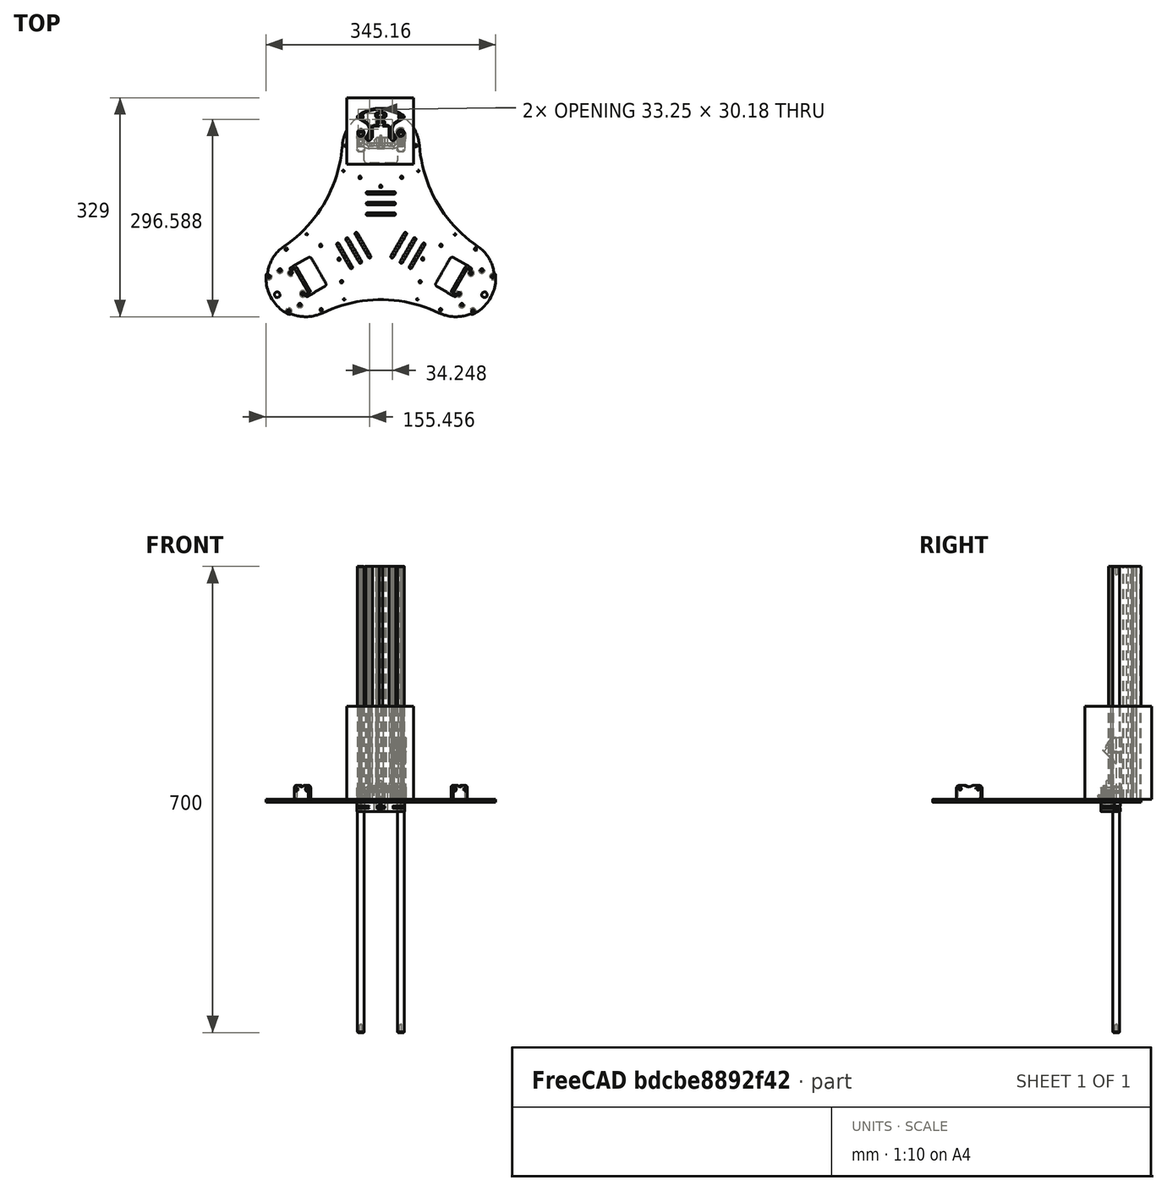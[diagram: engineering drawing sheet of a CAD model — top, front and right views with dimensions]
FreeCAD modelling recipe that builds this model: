
FCSTD DOCUMENT  (FreeCAD 0.18R16146 (Git))
Label: Vertical-Slider_w_FlyingExtruder
License: All rights reserved
LicenseURL: http://en.wikipedia.org/wiki/All_rights_reserved
objects: Part::FeaturePython×10, Part::Feature×9, App::Part×5, Sketcher::SketchObject×4, PartDesign::Plane×3, PartDesign::Body×3, Spreadsheet::Sheet×2, PartDesign::Revolution×1, Part::Box×1, Part::Compound×1, App::DocumentObjectGroup×1, PartDesign::Point×1, PartDesign::AdditiveLoft×1, Part::Mirroring×1, PartDesign::Hole×1, PartDesign::FeatureBase×1
note: 40 computed .brp shape members not serialized (recipe doc carries the construction recipe); baked Part::Feature solids carry a one-line shape summary decoded from their .brp

FEATURE [Part::Feature] K8800_BAP
  Placement = pos=(0,-153,-2) rot=(0,0,1;0rad)
  shape: bbox 351.2 x 331.3 x 25.02 mm, 225 faces (baked)
FEATURE [Part::Feature] K8800_RD10  label="K8800_RodLeft"
  Placement = pos=(-30,0,0) rot=(0,0,1;0rad)
  shape: bbox 10 x 10 x 700 mm, 9 faces (baked)
FEATURE [Part::Feature] K8800_RD011  label="K8800_RodRight"
  Placement = pos=(30,0,0) rot=(0,0,1;0rad)
  shape: bbox 10 x 10 x 700 mm, 9 faces (baked)
FEATURE [Part::Feature] K8800_RI
  shape: bbox 70.64 x 62.27 x 700 mm, 164 faces (baked)
FEATURE [Part::Feature] K8800_VS
  Placement = pos=(0,0,0) rot=(0,0,1;1.5708rad)
  shape: bbox 72.01 x 24.93 x 46.6 mm, 535 faces (baked)
FEATURE [Part::Feature] K8800_LB10  label="K8800_LB10-L"
  Placement = pos=(-30,0,0) rot=(0,0,1;0rad)
  shape: bbox 12 x 12 x 36 mm, 16 faces (baked)
FEATURE [Part::Feature] K8800_LB10001  label="K8800_LB10-R"
  Placement = pos=(30,0,0) rot=(0,0,1;0rad)
  shape: bbox 12 x 12 x 36 mm, 16 faces (baked)
FEATURE [Spreadsheet::Sheet] Spreadsheet  label="Schrauben"
  cells = A1(M5RadiusBore)==2.5mm; B1=M5RadiusBore; C1=Radius der Bohrungen für M5-Schrauben; A2(M5HexNutWidth)==8mm; B2=M5HexNutWidth; C2=Schlüsselweite der M5-Muttern; A3(M5HexNutHeight)==4mm; B3=M5HexNutHeight; C3=Höhe der M5-Muttern; A4(M5HexHeadRadius)==4.7mm; B4=M5HexHeadRadius; C4=Radius des Schraubenkopfes; A5(M5HexHeadHeight)==5.1mm; B5=M5HexHeadHeight; C5=Höhe des Schraubenkopfes; A6(M5InsertHeight)==6mm; B6=M5InsertHeight; C6=Höhe des Insert; A7(M5InserWidth)==6.3mm; B7=M5InserWidth; C7=Durchmesser (Taille) des Insert; A8(MCThreadLength)==8.25mm; B8=MCThreadLength; C8=Gewindelänge der Magnetic Cups; A9(MCHeadHeight)==4.8mm; B9=MCHeadHeight; C9=Kopfhöhe der Magentic Cups; A10(MCHeadRadius)==8.5mm / 2; B10=MCHeadRadius; C10=Radius des Magnetic Cups
FEATURE [Spreadsheet::Sheet] Spreadsheet001  label="Global"
  cells = A1===========; B1=3D Druckparameter; C1===================================; A2(NozzleSize)==0.6mm; B2=NozzleSize; C2=Düsendurchmesser; A3(ExtMult)=0.9; B3=ExtMult; C3=Extrusion Multiplier; A4(NozzleWidth)==NozzleSize * ExtMult; B4=NozzeWidth; C4=Extrusion width; A5(numPerimeter)=3; B5=numPerimeter; C5=Anzahl der Perimeter; A6(Flesh)==2 * NozzleWidth; B6=Flesh; C6=Zusätzlicher Material; A7===========; B7=Bronzelager; C7===================================; A8(bearingID)==10mm; B8=bearingID; C8=Innendurchmesser Lager; A9(bearingOD)==13mm; B9=bearingOD; C9=Außendurchmesser Lager; A10(bearingLen)==20mm; B10=bearingLen; C10=Länge des Lagers; A11===========; B11=Mechanik Lager; C11===================================; A12(distRods)==60mm; B12=distRods; C12=Abstand der Wellen; A13(diaRods)==10mm; B13=diaRods; C13=Durchmesser der Wellen; A14(clearanceRods)==NozzleWidth / 2; B14=clearanceRods; C14=Sicherheitsabstand für diaRods; A15===========; B15=Laufbuchse; C15===================================; A16(bushingShrink)==NozzleWidth / 2; B16=bushingShrink; C16=radiale Schrumpfung für Laufbuchsen-Pressung; A17(bushingID)==bearingOD; B17=bushingID; C17=Innendurchmesser Laufbuchse; A18(bushingID3D)==bushingID - 2 * bushingShrink; B18=bushingID3D; C18=zu druckender Innendurchmesser Laufbuchse; A19(bushingOD3D)==bushingID3D + numPerimeter * NozzleWidth * 2; B19=bushingOD3D; C19=zu druckender Außendurchmesser Laufbuchse; A20(bushingIR3D)==bushingID3D / 2; B20=bushingIR3D; C20=effektiver innerer Radius der Laufbuchse; A21(bushingOR3D)==bushingOD3D / 2; B21=bushingOR3D; C21=effektiver äußerer Radius der Laufbuchse; A22(bushingWallTickness)==numPerimeter * NozzleWidth; B22=bushingWallTickness; C22=Wanddicke Laufbuchse; A23(bushingLength)==90mm; B23=bushingLength; C23=Gesamtlänge der Linearführung; A24(bushingRotArc)==300°; B24=bushingRotArc; C24=Rotationswinkel für Extrusion; A25===========; B25=Vertical Slider; C25===================================; A32===========; C32===================================; A33===========; C33===================================; A34===========; C34===================================; A35===========; C35===================================; A36===========; C36===================================; A37===========; C37===================================
FEATURE [Part::Feature] K8800_MC  label="K8800_MC-L"
  Placement = pos=(-30,-18,-3.1e-15) rot=(1,0,0;1.5708rad)
  shape: bbox 8.5 x 12.91 x 8.5 mm, 20 faces (baked)
FEATURE [Part::Feature] K8800_MC001  label="K8800_MC-R"
  Placement = pos=(30,-18,-3.1e-15) rot=(1,0,0;1.5708rad)
  shape: bbox 8.5 x 12.91 x 8.5 mm, 20 faces (baked)
FEATURE [Sketcher::SketchObject] Sketch
  MapMode = 5
  Placement = pos=(0,0,0) rot=(1,0,0;1.5708rad)
  Support = -> [XZ_Plane003]
  expr: Constraints[12] = <<Global>>.bushingWallTickness
  expr: Constraints[11] = <<Global>>.bushingWallTickness
  sketch-geometry (13):
    g0: LineSegment [constr] StartX=0 StartY=50 StartZ=0 EndX=0 EndY=-50 EndZ=0
    g1: LineSegment StartX=-6.23 StartY=48.24 StartZ=0 EndX=-6.23 EndY=27.16 EndZ=0
    g2: LineSegment StartX=-7.85 StartY=48.24 StartZ=0 EndX=-7.85 EndY=27.16 EndZ=0
    g3: LineSegment StartX=-5.54 StartY=25 StartZ=0 EndX=-5.54 EndY=-25 EndZ=0
    g4: LineSegment StartX=-7.16 StartY=25 StartZ=0 EndX=-7.16 EndY=-25 EndZ=0
    g5: LineSegment StartX=-7.85 StartY=-27.16 StartZ=0 EndX=-7.85 EndY=-48.24 EndZ=0
    g6: LineSegment StartX=-6.23 StartY=-27.16 StartZ=0 EndX=-6.23 EndY=-48.24 EndZ=0
    g7: LineSegment StartX=-7.85 StartY=-48.24 StartZ=0 EndX=-6.23 EndY=-48.24 EndZ=0
    g8: LineSegment StartX=-7.85 StartY=48.24 StartZ=0 EndX=-6.23 EndY=48.24 EndZ=0
    g9: LineSegment StartX=-7.85 StartY=27.16 StartZ=0 EndX=-7.16 EndY=25 EndZ=0
    g10: LineSegment StartX=-6.23 StartY=27.16 StartZ=0 EndX=-5.54 EndY=25 EndZ=0
    g11: LineSegment StartX=-7.16 StartY=-25 StartZ=0 EndX=-7.85 EndY=-27.16 EndZ=0
    g12: LineSegment StartX=-5.54 StartY=-25 StartZ=0 EndX=-6.23 EndY=-27.16 EndZ=0
  constraints (39):
    c: Vertical(g0)
    c: DistanceY(g0,g0) = 100
    c: Symmetric(g0,g0,g-1)
    c: Vertical(g1)
    c: Vertical(g2)
    c: Vertical(g3)
    c: Vertical(g4)
    c: Vertical(g5)
    c: Vertical(g6)
    c: Horizontal(g7)
    c: Perpendicular(g8,g0)
    c: DistanceX(g8,g8) = 1.62
    c: DistanceX(g7,g7) = 1.62
    c: Coincident(g7,g6)
    c: Coincident(g7,g5)
    c: Coincident(g2,g8)
    c: Coincident(g1,g8)
    c: DistanceX(g4,g3) = 1.62
    c: DistanceY(g2,g2) = 21.08  'upperBushingLeft'
    c: DistanceY(g1,g1) = 21.08  'upperBushingRight'
    c: DistanceY(g5,g5) = 21.08  'lowerBushingLeft'
    c: DistanceY(g6,g6) = 21.08  'lowerBushingRight'
    c: DistanceY(g4,g4) = 50
    c: Equal(g4,g3)
    c: DistanceY(g3,g-1) = 25
    c: DistanceY(g4,g-1) = 25
    c: DistanceX(g1,g0) = 6.23
    c: DistanceX(g6,g-1) = 6.23
    c: DistanceY(g3,g1) = 2.16
    c: Coincident(g1,g10)
    c: Coincident(g10,g3)
    c: Coincident(g9,g2)
    c: Coincident(g9,g4)
    c: DistanceY(g12,g12) = 2.16
    c: Coincident(g12,g3)
    c: Coincident(g11,g4)
    c: DistanceX(g3,g-1) = 5.54
    c: Coincident(g12,g6)
    c: Coincident(g11,g5)
FEATURE [PartDesign::Revolution] Revolution
  Angle = 300
  Axis = (0,-2e-16,1)
  Base = (0,0,0)
  Placement = pos=(0,0,0) rot=(1,0,0;1.5708rad)
  Profile = -> Sketch
  ReferenceAxis = -> Sketch [V_Axis]
  expr: Angle = <<Global>>.bushingRotArc
FEATURE [App::Part] Part003  label="Velleman CAD"
  Group = -> [K8800_VS,K8800_LB10,K8800_LB10001,K8800_MC,K8800_MC001]
  Origin = -> Origin005
FEATURE [App::Part] Part  label="K8800-VerticalSlider"
  Group = -> [Part003]
  Origin = -> Origin
FEATURE [Part::Box] Box  label="Cube"
  AttacherType = Attacher::AttachEngine3D
  Height = 140
  Length = 100
  Placement = pos=(-51,-47,0) rot=(0,0,1;0rad)
  Width = 100
FEATURE [App::Part] Part004  label="Velleman CAD001"
  Origin = -> Origin006
FEATURE [Part::Compound] Compound
  Links = -> [K8800_RI,K8800_RD011,K8800_RD10]
FEATURE [Part::FeaturePython] Slice  # WARN: FeaturePython — macro-defined, semantics opaque (R4)
  Base = -> Compound
  Mode = 1
  Tolerance = 0
  Tools = -> [Box]
  Visibility1 = false
FEATURE [Part::FeaturePython] Slice_child0  label="Slice.0"  # WARN: FeaturePython — macro-defined, semantics opaque (R4)
  Base = -> Slice
  FilterType = 1
  Invert = false
  OverrideMaxVal = 0
  Visibility1 = false
  WindowFrom = 80
  WindowTo = 100
  items = 0
FEATURE [Part::FeaturePython] Slice_child1  label="Slice.1"  # WARN: FeaturePython — macro-defined, semantics opaque (R4)
  Base = -> Slice
  FilterType = 1
  Invert = false
  OverrideMaxVal = 0
  Visibility1 = true
  WindowFrom = 80
  WindowTo = 100
  items = 1
FEATURE [Part::FeaturePython] Slice_child2  label="Slice.2"  # WARN: FeaturePython — macro-defined, semantics opaque (R4)
  Base = -> Slice
  FilterType = 1
  Invert = false
  OverrideMaxVal = 0
  Visibility1 = false
  WindowFrom = 80
  WindowTo = 100
  items = 2
FEATURE [Part::FeaturePython] Slice_child3  label="Slice.3"  # WARN: FeaturePython — macro-defined, semantics opaque (R4)
  Base = -> Slice
  FilterType = 1
  Invert = false
  OverrideMaxVal = 0
  Visibility1 = false
  WindowFrom = 80
  WindowTo = 100
  items = 3
FEATURE [Part::FeaturePython] Slice_child4  label="Slice.4"  # WARN: FeaturePython — macro-defined, semantics opaque (R4)
  Base = -> Slice
  FilterType = 1
  Invert = false
  OverrideMaxVal = 0
  Visibility1 = true
  WindowFrom = 80
  WindowTo = 100
  items = 4
FEATURE [Part::FeaturePython] Slice_child5  label="Slice.5"  # WARN: FeaturePython — macro-defined, semantics opaque (R4)
  Base = -> Slice
  FilterType = 1
  Invert = false
  OverrideMaxVal = 0
  Visibility1 = false
  WindowFrom = 80
  WindowTo = 100
  items = 5
FEATURE [Part::FeaturePython] Slice_child6  label="Slice.6"  # WARN: FeaturePython — macro-defined, semantics opaque (R4)
  Base = -> Slice
  FilterType = 1
  Invert = false
  OverrideMaxVal = 0
  Visibility1 = false
  WindowFrom = 80
  WindowTo = 100
  items = 6
FEATURE [Part::FeaturePython] Slice_child7  label="Slice.7"  # WARN: FeaturePython — macro-defined, semantics opaque (R4)
  Base = -> Slice
  FilterType = 1
  Invert = false
  OverrideMaxVal = 0
  Visibility1 = true
  WindowFrom = 80
  WindowTo = 100
  items = 7
FEATURE [Part::FeaturePython] Slice_child8  label="Slice.8"  # WARN: FeaturePython — macro-defined, semantics opaque (R4)
  Base = -> Slice
  FilterType = 1
  Invert = false
  OverrideMaxVal = 0
  Visibility1 = false
  WindowFrom = 80
  WindowTo = 100
  items = 8
FEATURE [App::DocumentObjectGroup] GrExplode_Slice  label="Exploded Slice"
  Group = -> [Slice_child0,Slice_child1,Slice_child2,Slice_child3,Slice_child4,Slice_child5,Slice_child6,Slice_child7,Slice_child8]
FEATURE [App::Part] Part001  label="VerticalRods"
  Group = -> [Part004,Box,K8800_RI,K8800_RD011,K8800_RD10,Compound,Slice,Slice_child1,Slice_child7,Slice_child6,Slice_child0,Slice_child2,Slice_child3,Slice_child5,Slice_child4,Slice_child8,GrExplode_Slice]
  Origin = -> Origin001
  Placement = pos=(0,0,-20) rot=(0,0,1;0rad)
FEATURE [Sketcher::SketchObject] Sketch004
  AttachmentOffset = pos=(0,1,7.85) rot=(0,0,1;0rad)
  MapMode = 5
  Placement = pos=(0,-7.85,1) rot=(1,0,0;1.5708rad)
  Support = -> [XZ_Plane022]
  sketch-geometry (5):
    g0: Ellipse CenterX=-30 CenterY=66 CenterZ=0 NormalX=0 NormalY=0 NormalZ=1 MajorRadius=16 MinorRadius=7 AngleXU=-1.5708
    g1: LineSegment [constr] StartX=-30 StartY=50 StartZ=0 EndX=-30 EndY=82 EndZ=0
    g2: LineSegment [constr] StartX=-23 StartY=66 StartZ=0 EndX=-37 EndY=66 EndZ=0
    g3: GeomPoint X=-30 Y=51.6125 Z=0
    g4: GeomPoint X=-30 Y=80.3875 Z=0
  constraints (6):
    c: InternalAlignment(g1-g4 -> g0) x4
    c: DistanceX(g0,g-1) = 30
    c: DistanceX(g2,g2) = 14
    c: DistanceY(g1,g1) = 32
    c: DistanceY(g-1,g2) = 66
    c: Parallel(g1,g-2)
FEATURE [PartDesign::Point] DatumPoint
  AttacherType = Attacher::AttachEnginePoint
  MapMode = 37
  Placement = pos=(-30,-7.85,67.045) rot=(0,0,1;0rad)
  Support = -> [Sketch004]
FEATURE [Sketcher::SketchObject] Sketch005
  ExternalGeometry = -> [DatumPoint]
  MapMode = 5
  Placement = pos=(0,0,0) rot=(1,0,0;1.5708rad)
  Support = -> [XZ_Plane022]
  expr: Constraints[7] = Global.distRods / 2
  expr: Constraints[6] = <<Global>>.bushingOD3D - 1.5mm
  sketch-geometry (5):
    g0: LineSegment StartX=-37.1 StartY=83.045 StartZ=0 EndX=-22.9 EndY=83.045 EndZ=0
    g1: LineSegment StartX=-22.9 StartY=83.045 StartZ=0 EndX=-22.9 EndY=43.045 EndZ=0
    g2: LineSegment StartX=-22.9 StartY=43.045 StartZ=0 EndX=-37.1 EndY=43.045 EndZ=0
    g3: LineSegment StartX=-37.1 StartY=43.045 StartZ=0 EndX=-37.1 EndY=83.045 EndZ=0
    g4: LineSegment [constr] StartX=-30 StartY=83.045 StartZ=0 EndX=-30 EndY=32.845 EndZ=0
  constraints (14):
    c: Coincident(g0,g1)
    c: Coincident(g1,g2)
    c: Coincident(g2,g3)
    c: Coincident(g3,g0)
    c: Horizontal(g2)
    c: Vertical(g1)
    c: DistanceX(g0,g0) = 14.2
    c: DistanceX(g4,g-1) = 30
    c: Symmetric(g1,g2,g4)
    c: Symmetric(g0,g0,g4)
    c: Distance(g4) = 50.2
    c: DistanceY(g-3,g4) = 16
    c: DistanceY(g0,g4) = 0
    c: Distance(g0,g1) = 40
FEATURE [PartDesign::Plane] DatumPlane
  Length = 59.9116
  MapMode = 1
  Placement = pos=(-30,-7.85,67.045) rot=(1,0,0;-0.785398rad)
  ResizeMode = 0
  Support = -> [DatumPoint]
  Width = 99.9335
FEATURE [Sketcher::SketchObject] Sketch006
  AttachmentOffset = pos=(0,6,-11) rot=(0,0,1;0rad)
  MapMode = 5
  Placement = pos=(-30,-11.3855,55.0242) rot=(-1,0,0;0.785398rad)
  Support = -> [DatumPlane]
  sketch-geometry (1):
    g0: Circle CenterX=0 CenterY=-6.95 CenterZ=0 NormalX=0 NormalY=0 NormalZ=1 AngleXU=0 Radius=5.5
  constraints (3):
    c: Radius(g0) = 5.5
    c: DistanceY(g0,g-1) = 6.95
    c: DistanceX(g-1,g0) = 0
FEATURE [PartDesign::AdditiveLoft] AdditiveLoft
  Closed = false
  Placement = pos=(0,0,0) rot=(1,0,0;1.5708rad)
  Profile = -> Sketch005
  Ruled = true
  Sections = -> [Sketch004,Sketch006]
FEATURE [PartDesign::Plane] DatumPlane001
  AttachmentOffset = pos=(-20,-80,-7.85) rot=(0,0,1;0rad)
  Length = 40
  MapMode = 3
  Placement = pos=(-50,-3.02e-14,-12.955) rot=(1,0,0;1.5708rad)
  ResizeMode = 1
  Support = -> [DatumPoint]
  Width = 100
  expr: AttachmentOffset.Base.z = -Global.bushingOR3D
FEATURE [PartDesign::Plane] DatumPlane002
  AttachmentOffset = pos=(0,0,-1) rot=(0,0,1;0rad)
  Length = 37.5887
  MapMode = 45
  Placement = pos=(0.244953,-0.141423,2.7e-15) rot=(0.774597,0.447214,0.447214;1.82348rad)
  ResizeMode = 0
  Support = -> [Revolution]
  Width = 106.748
FEATURE [PartDesign::Body] Body  label="bearing (links)"
  Group = -> [Sketch,Revolution,DatumPlane002]
  Origin = -> Origin003
  Placement = pos=(-30,0,45) rot=(0,0,1;0rad)
  Tip = -> Revolution
FEATURE [Part::Mirroring] Part__Mirroring  label="bearing (rechts)"
  Base = (0,0,0)
  Normal = (1,0,0)
  Source = -> Body
FEATURE [PartDesign::Hole] Hole
  BaseFeature = -> AdditiveLoft
  Depth = 11
  DepthType = 0
  Diameter = 5
  DrillPoint = 0
  DrillPointAngle = 118
  HoleCutCountersinkAngle = 90
  HoleCutDepth = 7.5
  HoleCutDiameter = 6.3
  HoleCutType = 1
  ModelActualThread = false
  Placement = pos=(0,0,0) rot=(1,0,0;1.5708rad)
  Profile = -> AdditiveLoft [Face9]
  Tapered = false
  TaperedAngle = 90
  ThreadAngle = 0
  ThreadClass = 0
  ThreadCutOffInner = 0
  ThreadCutOffOuter = 0
  ThreadDirection = 0
  ThreadFit = 0
  ThreadPitch = 0
  ThreadSize = 0
  ThreadType = 0
  Threaded = false
  expr: Depth = Schrauben.MCThreadLength + 2.75mm
  expr: HoleCutDepth = Schrauben.M5InsertHeight + 1.5mm
  expr: HoleCutDiameter = Schrauben.M5InserWidth
  expr: Diameter = Schrauben.M5RadiusBore * 2
FEATURE [PartDesign::Body] Body017  label="Gelenkkopf (links)"
  Group = -> [Sketch004,Sketch005,DatumPoint,DatumPlane,Sketch006,AdditiveLoft,DatumPlane001,Hole]
  Origin = -> Origin022
  Placement = pos=(0,0,10) rot=(0,0,1;0rad)
  Tip = -> Hole
FEATURE [PartDesign::FeatureBase] Clone
  BaseFeature = -> Body017
  Placement = pos=(0,0,10) rot=(0,0,1;0rad)
FEATURE [PartDesign::Body] Body019  label="Gelenkkopf (rechts)"
  Group = -> [Clone]
  Origin = -> Origin024
  Placement = pos=(60,0,0) rot=(0,0,1;0rad)
  Tip = -> Clone
  expr: Placement.Base.x = Global.distRods
FEATURE [App::Part] Part002  label="Vertex Delta K8800"
  Group = -> [Part,K8800_BAP,Part001,Body,Body017,Body019,Part__Mirroring]
  Origin = -> Origin002
